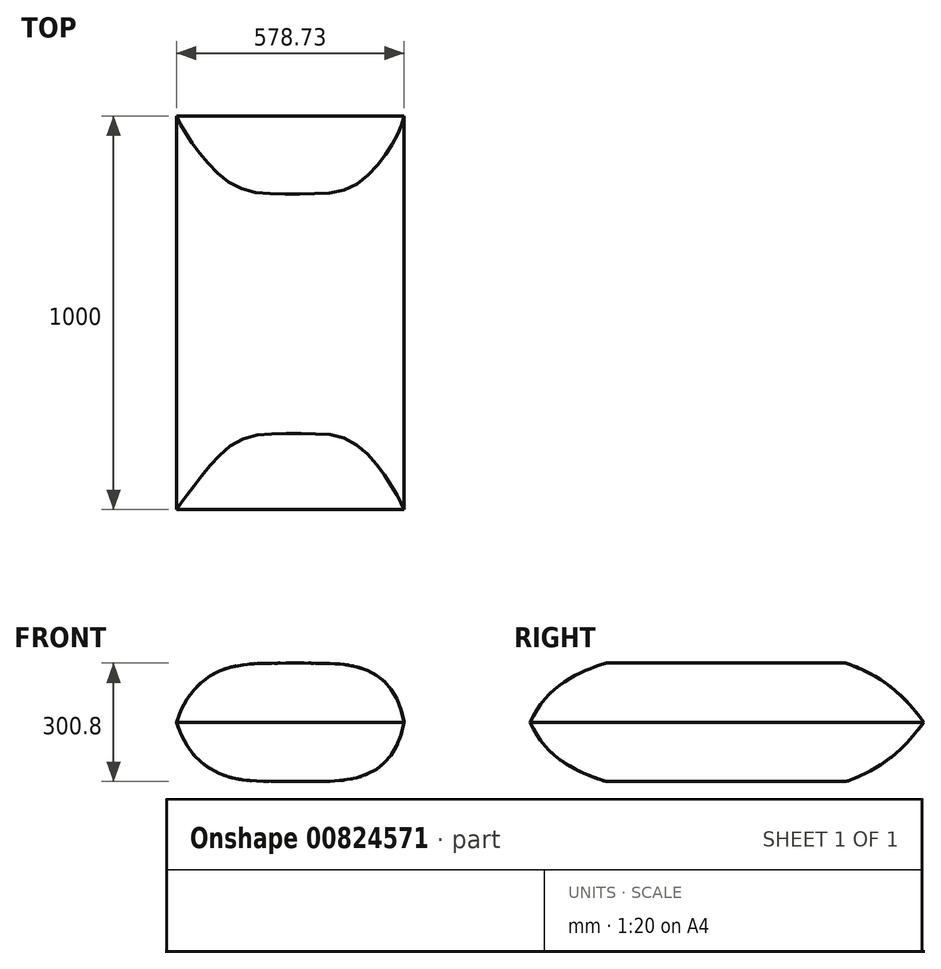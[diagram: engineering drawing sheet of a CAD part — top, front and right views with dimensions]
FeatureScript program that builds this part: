
annotation { "Feature Type Name" : "Feature", "Feature Type Description" : "" }
export const myFeature = defineFeature(function(context is Context, id is Id, definition is map)
    precondition{}
    {
        {
            var Q0;
            Q0=qCreatedBy(makeId("Front.planeOp"),FACE);
            var sketch = newSketch(context, id + "F0", { "sketchPlane" : qUnion([Q0])});
            skFitSpline(sketch, "E0", {"points": [v(0, 0) * mm, v(235.4, 150) * mm, v(364.6, 150) * mm, v(578.73, 0) * mm], "startDerivative": vector(381.93, 1170.52) * mm, "endDerivative": vector(220.03, -1209.47) * mm});
            skLineSegment(sketch, "E1", {"start": v(300, 0) * mm, "end": v(300, 221.36) * mm, "construction": true});
            skLineSegment(sketch, "E2", {"start": v(300, 0) * mm, "end": v(653.95, 0) * mm, "construction": true});
            skFitSpline(sketch, "E3.MirrorCS", {"points": [v(0, 0) * mm, v(235.4, -150) * mm, v(364.6, -150) * mm, v(578.73, 0) * mm], "startDerivative": vector(381.93, -1170.52) * mm, "endDerivative": vector(220.03, 1209.47) * mm});
            skSolve(sketch);
        }
        {
            var Q0;
            Q0=makeQuery(id+"F0.imprint","IMPRINT",FACE,{"disambiguationData":[TD([[makeQuery(id+"F0.imprint","IMPRINT",EDGE,{"derivedFrom":sQuery(id+"F0.wireOp",EDGE,"E0")}),-1.0]])]});
            extrude(context, id + "F1", {"entities" : qUnion([Q0]), "depth" : 1000 * mm, "offsetDistance" : 25 * mm});
        }
        {
            var Q0;
            Q0=qCreatedBy(makeId("Right.planeOp"),FACE);
            var sketch = newSketch(context, id + "F2", { "sketchPlane" : qUnion([Q0])});
            skFitSpline(sketch, "E4", {"points": [v(0, 0) * mm, v(-228.92, 160) * mm, v(-771.08, 160) * mm, v(-1000, 0) * mm], "startDerivative": vector(-557.78, 780.47) * mm, "endDerivative": vector(-390.46, -881.79) * mm});
            skLineSegment(sketch, "E5", {"start": v(-500, 0) * mm, "end": v(-500, 223.76) * mm, "construction": true});
            skLineSegment(sketch, "E6", {"start": v(-500, 0) * mm, "end": v(-1168.34, 0) * mm, "construction": true});
            skFitSpline(sketch, "E7.MirrorCS", {"points": [v(0, 0) * mm, v(-228.92, -160) * mm, v(-771.08, -160) * mm, v(-1000, 0) * mm], "startDerivative": vector(-557.78, -780.47) * mm, "endDerivative": vector(-390.46, 881.79) * mm});
            skSolve(sketch);
        }
        {
            var Q0;
            Q0 = qSketchRegion(id + "F2", true);
            extrude(context, id + "F3", {"entities" : qUnion([Q0]), "operationType" : NewBodyOperationType.INTERSECT, "endBound" : BoundingType.THROUGH_ALL, "depth" : 25 * mm, "offsetDistance" : 25 * mm});
        }
    });
